# Revit family: Basin-Caroma Orbis Inset Vanity
name_source: partatom
category: Plumbing Fixtures
revit_build: Autodesk Revit Architecture 2012 (Build: 20110309_2315(x64)
units: mm (PartAtom-declared; Revit-internal decimal feet)

## types (2) — shared parameters
CW Connection = No
Default Elevation = 1219 mm
Description = Orbis Inset Vanity Basin
HW Connection = No
Manufacturer = Caroma
PlumbingMaterial_ANZRS = Porcelain-White-Caroma
Type Comments = Vitreous China Inset Vanity Basin
URL = www.caroma.com.au
Vent Connection = No
Waste = Metal-Chrome-Caroma
Waste Connection = Yes
zero-valued in all types: Spout Penetration

## per-type parameters (varying)
| type | 1 Taphole | 3 Tapholes | Model | Tap Penetrations |
| Orbis Inset - 3 Tap Holes | No | Yes | 633435 | 0 mm  [stored 0 ft] |
| Orbis Inset - 1 Tap Hole | Yes | No | 633415 | 100 mm  [stored 0.328084 ft] |

note: [stored X ft] marks values corroborated as IEEE doubles in the binary element streams (Revit-internal decimal feet)

## geometry (parser evidence)
native form markers: Blend x8, Sweep x1
no freeform markers — native parametric forms only
